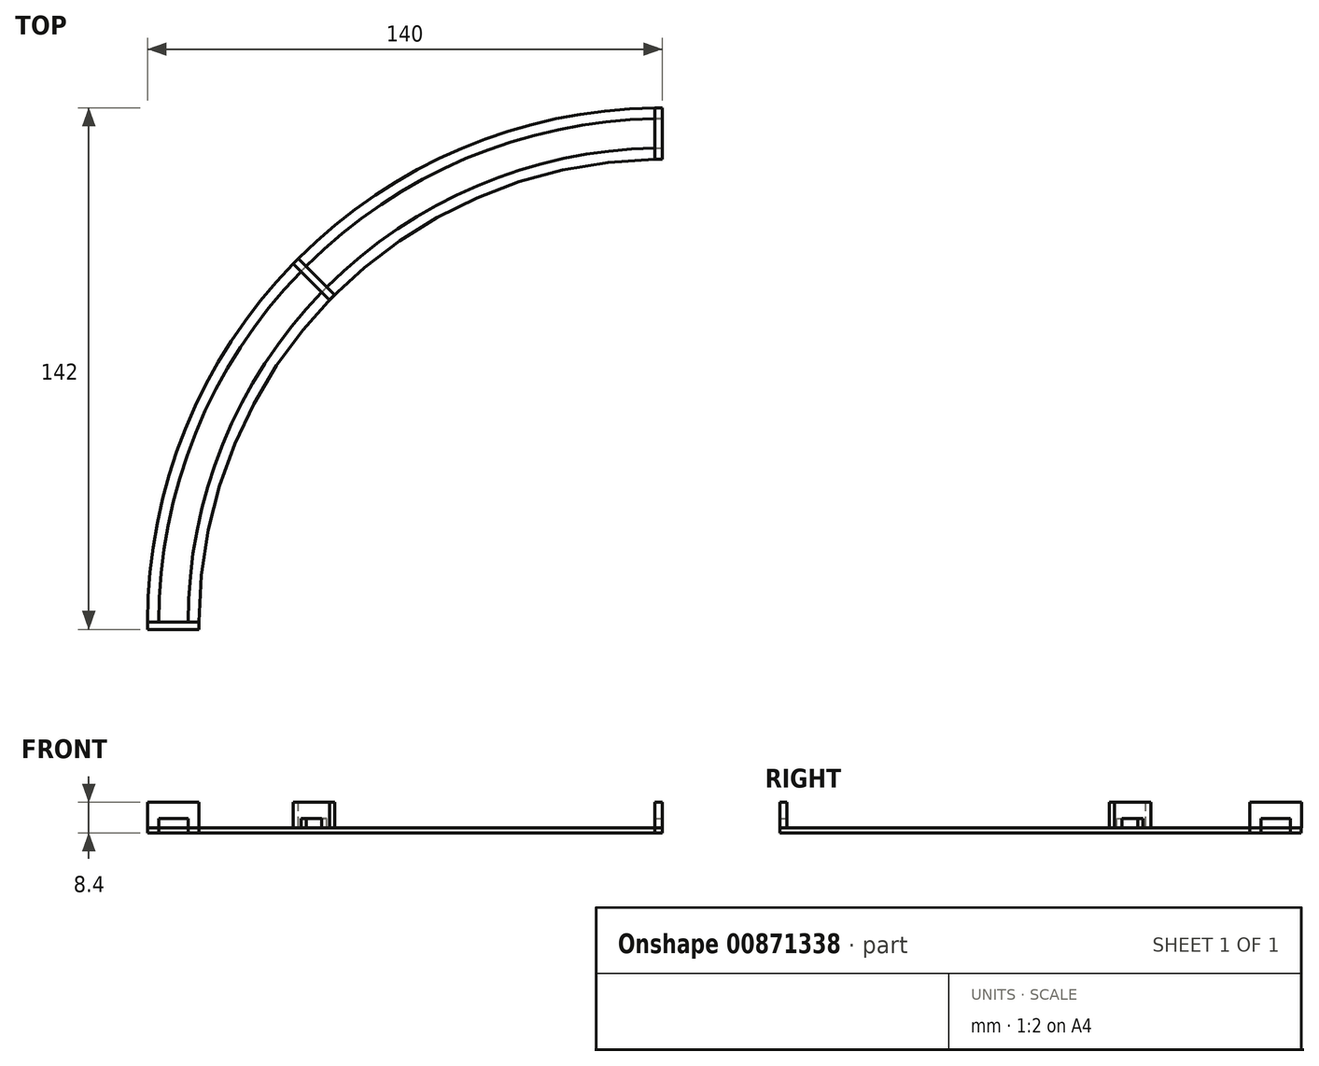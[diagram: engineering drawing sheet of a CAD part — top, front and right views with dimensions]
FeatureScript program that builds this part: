
annotation { "Feature Type Name" : "Feature", "Feature Type Description" : "" }
export const myFeature = defineFeature(function(context is Context, id is Id, definition is map)
    precondition{}
    {
        {
            var Q0;
            Q0=qCreatedBy(makeId("Top.planeOp"),FACE);
            var sketch = newSketch(context, id + "F0", { "sketchPlane" : qUnion([Q0])});
            skArc(sketch, "E0", {"start": v(-2, 139.99) * mm, "mid": v(-99.7, 98.29) * mm, "end": v(-140, 0) * mm});
            skArc(sketch, "E1.0", {"start": v(-2, 136.99) * mm, "mid": v(-97.58, 96.16) * mm, "end": v(-137, 0) * mm});
            skArc(sketch, "E2.0", {"start": v(-2, 128.98) * mm, "mid": v(-91.92, 90.5) * mm, "end": v(-129, 0) * mm});
            skArc(sketch, "E3.0", {"start": v(-2, 125.98) * mm, "mid": v(-89.8, 88.39) * mm, "end": v(-126, 0) * mm});
            skLineSegment(sketch, "E4", {"start": v(-140, 0) * mm, "end": v(-140, -2) * mm});
            skLineSegment(sketch, "E5", {"start": v(-140, -2) * mm, "end": v(-137, -2) * mm});
            skLineSegment(sketch, "E6", {"start": v(-137, -2) * mm, "end": v(-137, 0) * mm});
            skLineSegment(sketch, "E7", {"start": v(-129, 0) * mm, "end": v(-129, -2) * mm});
            skLineSegment(sketch, "E8", {"start": v(-129, -2) * mm, "end": v(-126, -2) * mm});
            skLineSegment(sketch, "E9", {"start": v(-126, -2) * mm, "end": v(-126, 0) * mm});
            skLineSegment(sketch, "E10", {"start": v(-2, 139.99) * mm, "end": v(0, 139.99) * mm});
            skLineSegment(sketch, "E11", {"start": v(0, 139.99) * mm, "end": v(0, 136.99) * mm});
            skLineSegment(sketch, "E12", {"start": v(0, 136.99) * mm, "end": v(-2, 136.99) * mm});
            skLineSegment(sketch, "E13", {"start": v(-2, 128.98) * mm, "end": v(0, 128.98) * mm});
            skLineSegment(sketch, "E14", {"start": v(0, 128.98) * mm, "end": v(0, 125.98) * mm});
            skLineSegment(sketch, "E15", {"start": v(0, 125.98) * mm, "end": v(-2, 125.98) * mm});
            skSolve(sketch);
        }
        {
            var Q0;
            Q0=makeQuery(id+"F0.imprint","IMPRINT",FACE,{"disambiguationData":[TD([[makeQuery(id+"F0.imprint","IMPRINT",EDGE,{"derivedFrom":sQuery(id+"F0.wireOp",EDGE,"E0")}),1.0]])]});
            var Q1;
            Q1=makeQuery(id+"F0.imprint","IMPRINT",FACE,{"disambiguationData":[TD([[makeQuery(id+"F0.imprint","IMPRINT",EDGE,{"derivedFrom":sQuery(id+"F0.wireOp",EDGE,"E2.0")}),1.0]])]});
            extrude(context, id + "F1", {"entities" : qUnion([Q0, Q1]), "depth" : 1.4 * mm, "offsetDistance" : 25 * mm});
        }
        {
            var Q0;
            Q0=qCreatedBy(makeId("Front.planeOp"),FACE);
            var sketch = newSketch(context, id + "F2", { "sketchPlane" : qUnion([Q0])});
            skLineSegment(sketch, "E16", {"start": v(-137, 3.9) * mm, "end": v(-137, 1.4) * mm});
            skLineSegment(sketch, "E17", {"start": v(-137, 1.4) * mm, "end": v(-140, 1.4) * mm});
            skLineSegment(sketch, "E18", {"start": v(-140, 1.4) * mm, "end": v(-140, 8.4) * mm});
            skLineSegment(sketch, "E19", {"start": v(-140, 8.4) * mm, "end": v(-126, 8.4) * mm});
            skLineSegment(sketch, "E20", {"start": v(-126, 8.4) * mm, "end": v(-126, 1.4) * mm});
            skLineSegment(sketch, "E21", {"start": v(-126, 1.4) * mm, "end": v(-129, 1.4) * mm});
            skLineSegment(sketch, "E22", {"start": v(-129, 1.4) * mm, "end": v(-129, 3.9) * mm});
            skLineSegment(sketch, "E23", {"start": v(-129, 3.9) * mm, "end": v(-137, 3.9) * mm});
            skSolve(sketch);
        }
        {
            var Q0;
            Q0=makeQuery(id+"F2.imprint","IMPRINT",FACE,{"disambiguationData":[TD([[makeQuery(id+"F2.imprint","IMPRINT",EDGE,{"derivedFrom":sQuery(id+"F2.wireOp",EDGE,"E16")}),-1.0]])]});
            extrude(context, id + "F3", {"entities" : qUnion([Q0]), "depth" : 2 * mm, "offsetDistance" : 25 * mm});
        }
        {
            var Q0;
            Q0=makeQuery(id+"F3.opExtrude","SWEPT_BODY",BODY,{"disambiguationData":[OSD([sQuery(id+"F2.wireOp",EDGE,"E16"),sQuery(id+"F2.wireOp",EDGE,"E17"),sQuery(id+"F2.wireOp",EDGE,"E18"),sQuery(id+"F2.wireOp",EDGE,"E19"),sQuery(id+"F2.wireOp",EDGE,"E20"),sQuery(id+"F2.wireOp",EDGE,"E21"),sQuery(id+"F2.wireOp",EDGE,"E22"),sQuery(id+"F2.wireOp",EDGE,"E23")])]});
            var Q1;
            Q1=makeQuery(id+"F1.opExtrude","SWEPT_FACE",FACE,{"disambiguationData":[OSD([sQuery(id+"F0.wireOp",EDGE,"E3.0")])]});
            circularPattern(context, id + "F4", {"entities" : qUnion([Q0]), "axis" : qUnion([Q1]), "angle" : 90 * degree, "instanceCount" : 3, "oppositeDirection" : true, "equalSpace" : true});
        }
    });
